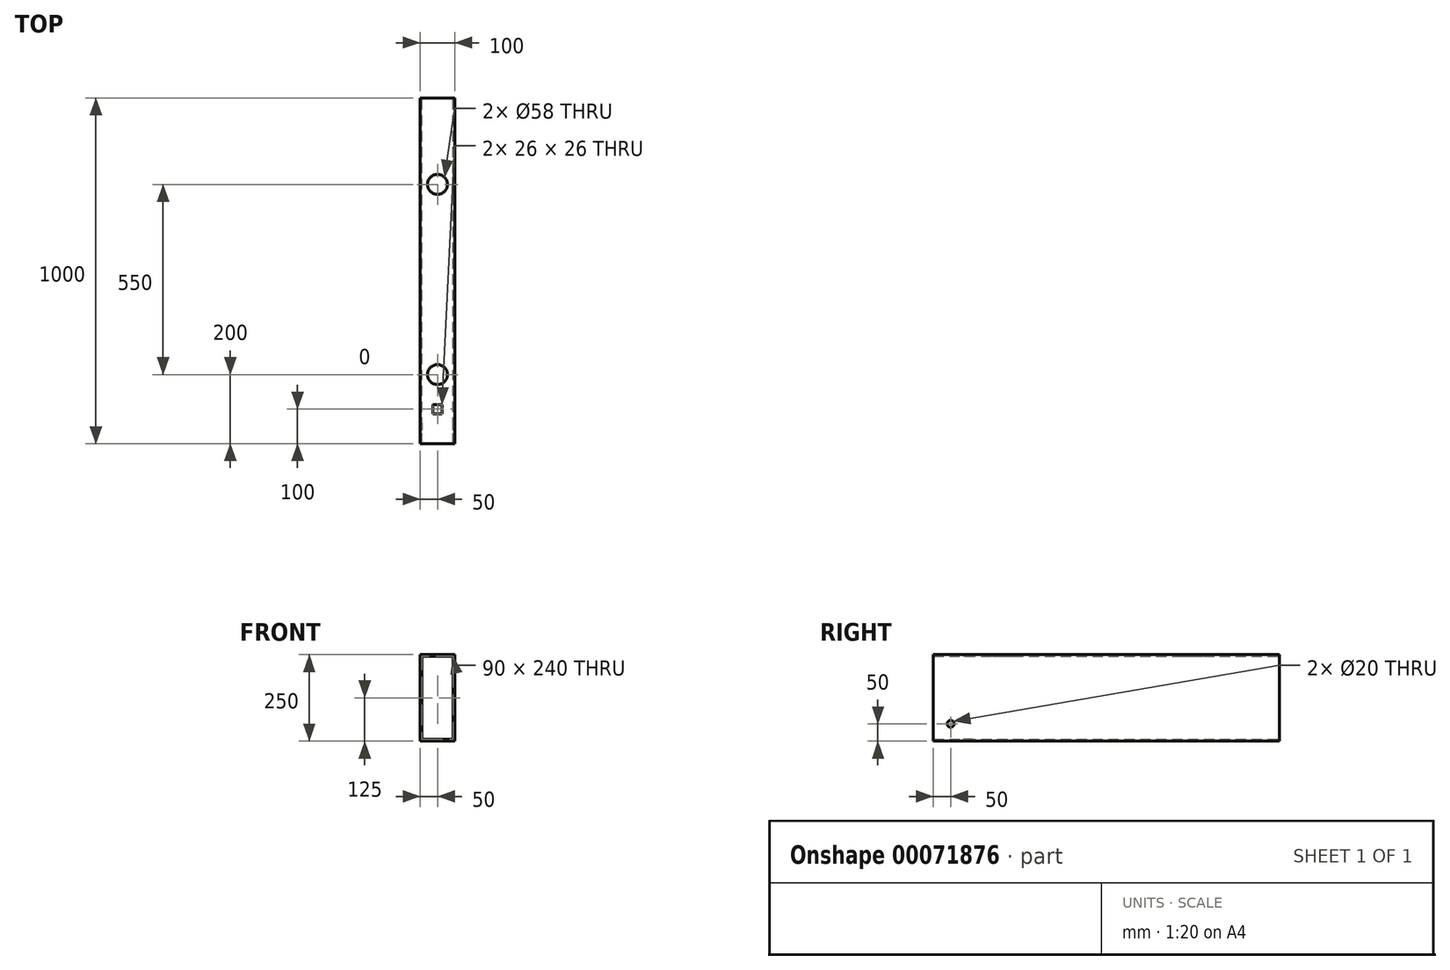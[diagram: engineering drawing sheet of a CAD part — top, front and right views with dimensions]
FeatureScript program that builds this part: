
annotation { "Feature Type Name" : "Feature", "Feature Type Description" : "" }
export const myFeature = defineFeature(function(context is Context, id is Id, definition is map)
    precondition{}
    {
        {
            var Q0;
            Q0=qCreatedBy(makeId("Front.planeOp"),FACE);
            var sketch = newSketch(context, id + "F0", { "sketchPlane" : qUnion([Q0])});
            skLineSegment(sketch, "E0.bottom", {"start": v(50, -125) * mm, "end": v(-50, -125) * mm});
            skLineSegment(sketch, "E0.top", {"start": v(50, 125) * mm, "end": v(-50, 125) * mm});
            skLineSegment(sketch, "E0.left", {"start": v(50, -125) * mm, "end": v(50, 125) * mm});
            skLineSegment(sketch, "E0.right", {"start": v(-50, -125) * mm, "end": v(-50, 125) * mm});
            skPoint(sketch, "E0.middle", {"position": v(0, 0) * mm});
            skLineSegment(sketch, "E1.bottom", {"start": v(-45, 120) * mm, "end": v(45, 120) * mm});
            skLineSegment(sketch, "E1.top", {"start": v(-45, -120) * mm, "end": v(45, -120) * mm});
            skLineSegment(sketch, "E1.left", {"start": v(-45, 120) * mm, "end": v(-45, -120) * mm});
            skLineSegment(sketch, "E1.right", {"start": v(45, 120) * mm, "end": v(45, -120) * mm});
            skSolve(sketch);
        }
        {
            var Q0;
            Q0=qSketchRegion(id+"F0",true);
            extrude(context, id + "F1", {"entities" : qUnion([Q0]), "depth" : 1000 * mm});
        }
        {
            var Q0;
            Q0=makeQuery(id+"F1.opExtrude","SWEPT_FACE",FACE,{"disambiguationData":[OSD([sQuery(id+"F0.wireOp",EDGE,"E0.left")])]});
            var sketch = newSketch(context, id + "F2", { "sketchPlane" : qUnion([Q0])});
            skCircle(sketch, "E2", {"center": v(-950, -75) * mm, "radius": 10 * mm});
            skSolve(sketch);
        }
        {
            var Q0;
            Q0=qSketchRegion(id+"F2",true);
            extrude(context, id + "F3", {"entities" : qUnion([Q0]), "operationType" : NewBodyOperationType.REMOVE, "endBound" : BoundingType.THROUGH_ALL, "oppositeDirection" : true, "depth" : 25 * mm});
        }
        {
            var Q0;
            Q0=makeQuery(id+"F1.opExtrude","SWEPT_FACE",FACE,{"disambiguationData":[OSD([sQuery(id+"F0.wireOp",EDGE,"E0.top")])]});
            var sketch = newSketch(context, id + "F4", { "sketchPlane" : qUnion([Q0])});
            skCircle(sketch, "E3", {"center": v(0, -800) * mm, "radius": 29 * mm});
            skSolve(sketch);
        }
        {
            var Q0;
            Q0=makeQuery(id+"F1.opExtrude","SWEPT_FACE",FACE,{"disambiguationData":[OSD([sQuery(id+"F0.wireOp",EDGE,"E0.top")])]});
            var sketch = newSketch(context, id + "F5", { "sketchPlane" : qUnion([Q0])});
            skCircle(sketch, "E4", {"center": v(0, -250) * mm, "radius": 29 * mm});
            skSolve(sketch);
        }
        {
            var Q0;
            Q0=qSketchRegion(id+"F4",true);
            var Q1;
            Q1=qSketchRegion(id+"F5",true);
            var Q2;
            Q2=qSketchRegion(id+"FMOpO3zPfPI2vzJ_1",true);
            extrude(context, id + "F6", {"entities" : qUnion([Q0, Q1, Q2]), "operationType" : NewBodyOperationType.REMOVE, "endBound" : BoundingType.UP_TO_NEXT, "oppositeDirection" : true, "depth" : 25 * mm});
        }
        {
            var Q0;
            Q0=makeQuery(id+"F1.opExtrude","SWEPT_FACE",FACE,{"disambiguationData":[OSD([sQuery(id+"F0.wireOp",EDGE,"E0.top")])]});
            var sketch = newSketch(context, id + "F7", { "sketchPlane" : qUnion([Q0])});
            skLineSegment(sketch, "E5.bottom", {"start": v(13, -887) * mm, "end": v(-13, -887) * mm});
            skLineSegment(sketch, "E5.top", {"start": v(13, -913) * mm, "end": v(-13, -913) * mm});
            skLineSegment(sketch, "E5.left", {"start": v(13, -887) * mm, "end": v(13, -913) * mm});
            skLineSegment(sketch, "E5.right", {"start": v(-13, -887) * mm, "end": v(-13, -913) * mm});
            skPoint(sketch, "E5.middle", {"position": v(0, -900) * mm});
            skSolve(sketch);
        }
        {
            var Q0;
            Q0 = qSketchRegion(id + "F7", true);
            extrude(context, id + "F8", {"entities" : qUnion([Q0]), "operationType" : NewBodyOperationType.REMOVE, "endBound" : BoundingType.THROUGH_ALL, "oppositeDirection" : true, "depth" : 25 * mm});
        }
    });
